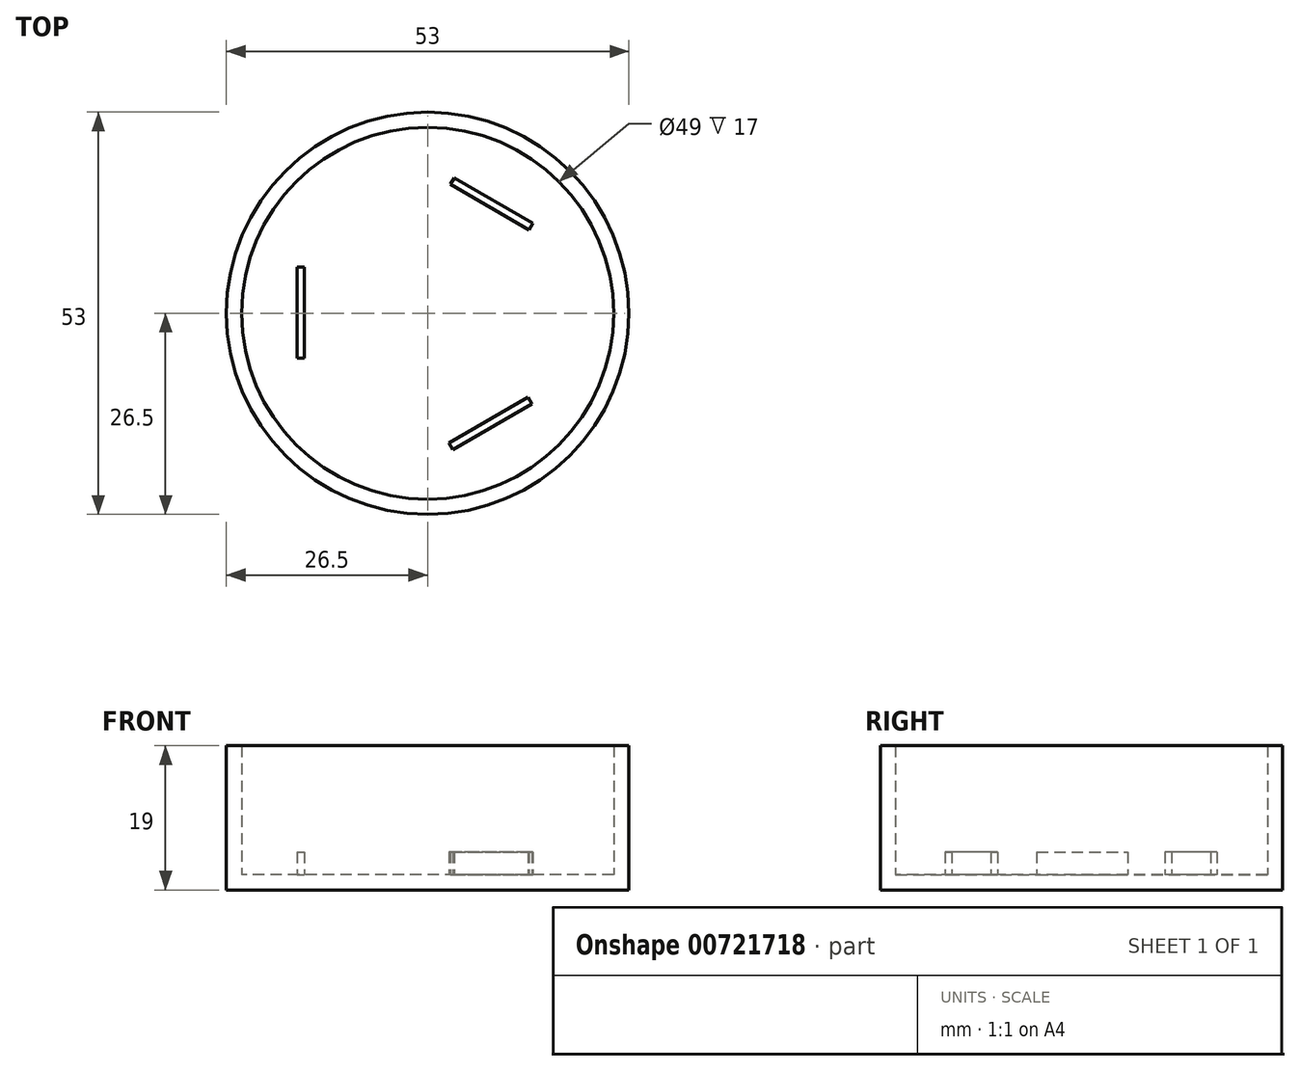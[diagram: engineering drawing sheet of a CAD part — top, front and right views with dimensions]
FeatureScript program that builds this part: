
annotation { "Feature Type Name" : "Feature", "Feature Type Description" : "" }
export const myFeature = defineFeature(function(context is Context, id is Id, definition is map)
    precondition{}
    {
        {
            var Q0;
            Q0=qCreatedBy(makeId("Top.planeOp"),FACE);
            var sketch = newSketch(context, id + "F0", { "sketchPlane" : qUnion([Q0])});
            skCircle(sketch, "E0", {"center": v(0, 0) * mm, "radius": 24.5 * mm});
            skSolve(sketch);
        }
        {
            var Q0;
            Q0 = qSketchRegion(id + "F0", true);
            extrude(context, id + "F1", {"entities" : qUnion([Q0]), "depth" : 17 * mm, "offsetDistance" : 25 * mm});
        }
        {
            var Q0;
            Q0=makeQuery(id+"F1.opExtrude","CAP_FACE",FACE,{"disambiguationData":[OSD([sQuery(id+"F0.wireOp",EDGE,"E0")])],"isStart":false});
            shell(context, id + "F2", {"entities" : qUnion([Q0]), "thickness" : 2 * mm, "oppositeDirection" : true});
        }
        {
            var Q0;
            {var subQ0=sQuery(id+"F0.wireOp",EDGE,"E0");Q0=makeQuery(id+"F2.opShell","OFFSET_FACE",FACE,{"disambiguationData":[OSD([subQ0]),TDD([makeQuery(id+"F1.opExtrude","CAP_FACE",FACE,{"disambiguationData":[OSD([subQ0])],"isStart":true})])]});}
            var sketch = newSketch(context, id + "F3", { "sketchPlane" : qUnion([Q0])});
            skLineSegment(sketch, "E1.bottom", {"start": v(-17.2, -5.9) * mm, "end": v(-16.2, -5.9) * mm});
            skLineSegment(sketch, "E1.top", {"start": v(-17.2, 6.1) * mm, "end": v(-16.2, 6.1) * mm});
            skLineSegment(sketch, "E1.left", {"start": v(-17.2, -5.9) * mm, "end": v(-17.2, 6.1) * mm});
            skLineSegment(sketch, "E1.right", {"start": v(-16.2, -5.9) * mm, "end": v(-16.2, 6.1) * mm});
            skLineSegment(sketch, "E2.1.0", {"start": v(13.71, -11.95) * mm, "end": v(13.21, -11.09) * mm});
            skLineSegment(sketch, "E2.1.1", {"start": v(13.71, -11.95) * mm, "end": v(3.32, -17.95) * mm});
            skLineSegment(sketch, "E2.1.2", {"start": v(3.32, -17.95) * mm, "end": v(2.82, -17.09) * mm});
            skLineSegment(sketch, "E2.1.3", {"start": v(13.21, -11.09) * mm, "end": v(2.82, -17.09) * mm});
            skLineSegment(sketch, "E2.2.0", {"start": v(3.5, 17.85) * mm, "end": v(3, 16.99) * mm});
            skLineSegment(sketch, "E2.2.1", {"start": v(3.5, 17.85) * mm, "end": v(13.89, 11.85) * mm});
            skLineSegment(sketch, "E2.2.2", {"start": v(13.89, 11.85) * mm, "end": v(13.39, 10.99) * mm});
            skLineSegment(sketch, "E2.2.3", {"start": v(3, 16.99) * mm, "end": v(13.39, 10.99) * mm});
            skPoint(sketch, "E2.center", {"position": v(0, 0) * mm});
            skSolve(sketch);
        }
        {
            var Q0;
            Q0 = qSketchRegion(id + "F3", true);
            extrude(context, id + "F4", {"entities" : qUnion([Q0]), "operationType" : NewBodyOperationType.ADD, "depth" : 3 * mm, "offsetDistance" : 25 * mm});
        }
    });
